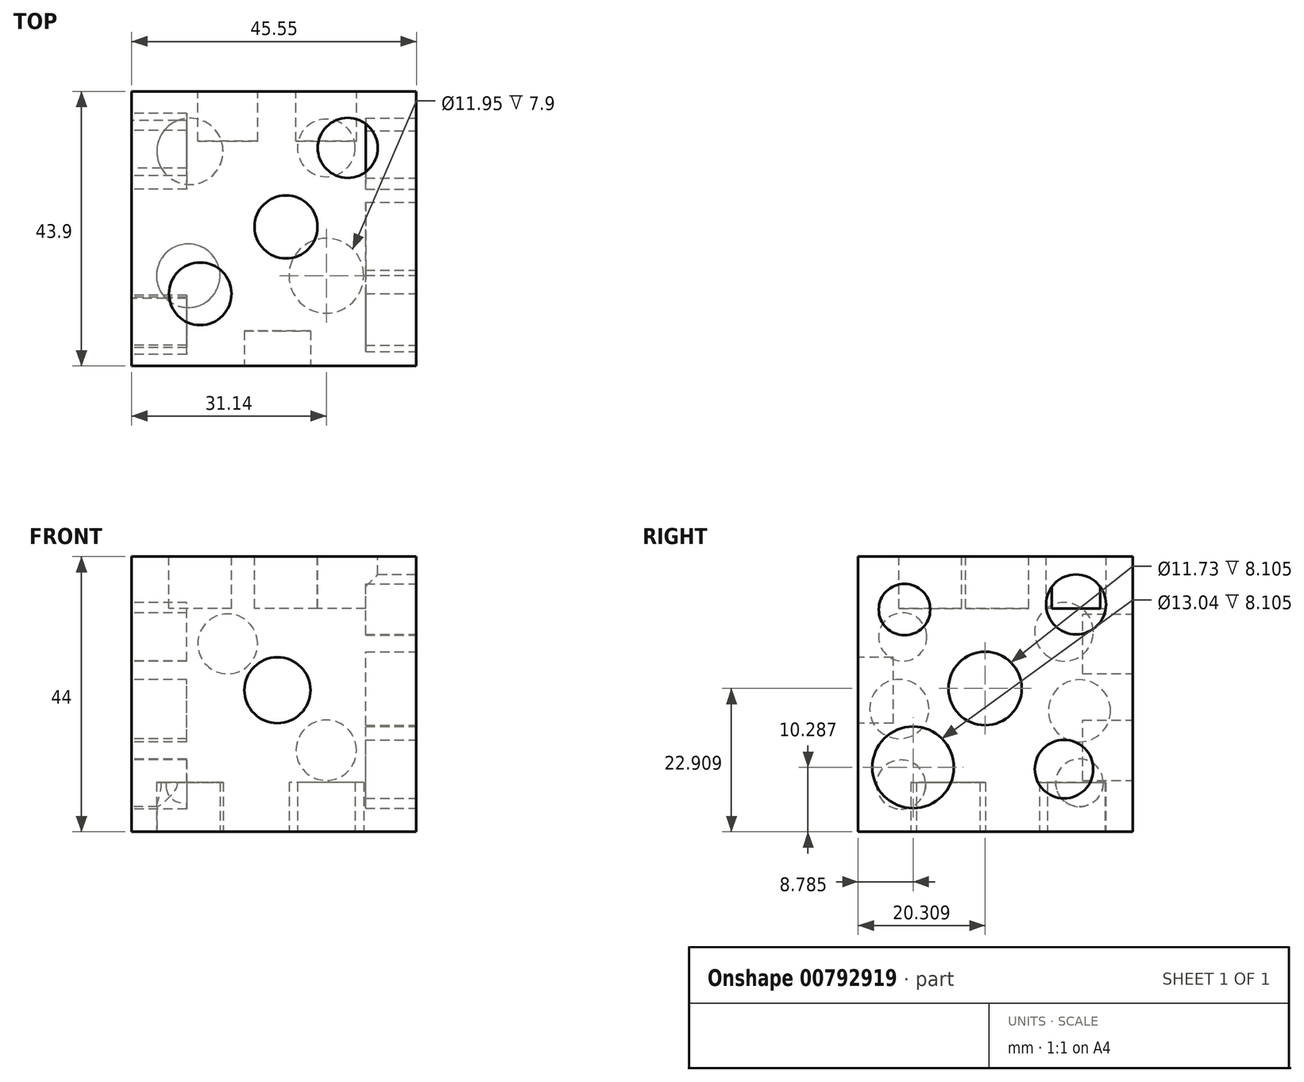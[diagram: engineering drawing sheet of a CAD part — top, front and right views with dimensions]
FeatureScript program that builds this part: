
annotation { "Feature Type Name" : "Feature", "Feature Type Description" : "" }
export const myFeature = defineFeature(function(context is Context, id is Id, definition is map)
    precondition{}
    {
        {
            var Q0;
            Q0=qCreatedBy(makeId("Top.planeOp"),FACE);
            var sketch = newSketch(context, id + "F0", { "sketchPlane" : qUnion([Q0])});
            skLineSegment(sketch, "E0.bottom", {"start": v(14.4, 29.5) * mm, "end": v(-31.14, 29.5) * mm});
            skLineSegment(sketch, "E0.top", {"start": v(14.4, -14.4) * mm, "end": v(-31.14, -14.4) * mm});
            skLineSegment(sketch, "E0.left", {"start": v(14.4, 29.5) * mm, "end": v(14.4, -14.4) * mm});
            skLineSegment(sketch, "E0.right", {"start": v(-31.14, 29.5) * mm, "end": v(-31.14, -14.4) * mm});
            skPoint(sketch, "E0.middle", {"position": v(-8.37, 7.54) * mm});
            skSolve(sketch);
        }
        {
            var Q0;
            Q0=makeQuery(id+"F0.imprint","IMPRINT",FACE,{"disambiguationData":[TD([[makeQuery(id+"F0.imprint","IMPRINT",EDGE,{"derivedFrom":sQuery(id+"F0.wireOp",EDGE,"E0.bottom")}),1.0]])]});
            extrude(context, id + "F1", {"entities" : qUnion([Q0]), "depth" : 44 * mm, "offsetDistance" : 25 * mm});
        }
        {
            var Q0;
            Q0=qCreatedBy(makeId("Front.planeOp"),FACE);
            cPlane(context, id + "F2", {"entities" : qUnion([Q0]), "cplaneType" : CPlaneType.OFFSET, "offset" : 14.9 * mm, "width" : 150 * mm, "height" : 150 * mm});
        }
        {
            var Q0;
            Q0=qCreatedBy(id+"F2.planeOp",FACE);
            var sketch = newSketch(context, id + "F3", { "sketchPlane" : qUnion([Q0])});
            skCircle(sketch, "E1", {"center": v(-7.82, 22.63) * mm, "radius": 5.28 * mm});
            skSolve(sketch);
        }
        {
            var Q0;
            Q0=makeQuery(id+"F3.imprint","IMPRINT",FACE,{"disambiguationData":[TD([[makeQuery(id+"F3.imprint","IMPRINT",EDGE,{"derivedFrom":sQuery(id+"F3.wireOp",EDGE,"E1")}),1.0]])]});
            extrude(context, id + "F4", {"entities" : qUnion([Q0]), "operationType" : NewBodyOperationType.REMOVE, "oppositeDirection" : true, "depth" : 6.1 * mm, "offsetDistance" : 25 * mm});
        }
        {
            var Q0;
            Q0=qCreatedBy(makeId("Front.planeOp"),FACE);
            cPlane(context, id + "F5", {"entities" : qUnion([Q0]), "cplaneType" : CPlaneType.OFFSET, "offset" : 30.2 * mm, "oppositeDirection" : true, "width" : 150 * mm, "height" : 150 * mm});
        }
        {
            var Q0;
            Q0=qCreatedBy(id+"F5.planeOp",FACE);
            var sketch = newSketch(context, id + "F6", { "sketchPlane" : qUnion([Q0])});
            skCircle(sketch, "E2", {"center": v(-15.78, 30.04) * mm, "radius": 4.8 * mm});
            skCircle(sketch, "E3", {"center": v(0, 13.03) * mm, "radius": 4.83 * mm});
            skSolve(sketch);
        }
        {
            var Q0;
            Q0=makeQuery(id+"F6.imprint","IMPRINT",FACE,{"disambiguationData":[TD([[makeQuery(id+"F6.imprint","IMPRINT",EDGE,{"derivedFrom":sQuery(id+"F6.wireOp",EDGE,"E2")}),1.0]])]});
            var Q1;
            Q1=makeQuery(id+"F6.imprint","IMPRINT",FACE,{"disambiguationData":[TD([[makeQuery(id+"F6.imprint","IMPRINT",EDGE,{"derivedFrom":sQuery(id+"F6.wireOp",EDGE,"E3")}),1.0]])]});
            extrude(context, id + "F7", {"entities" : qUnion([Q0, Q1]), "operationType" : NewBodyOperationType.REMOVE, "depth" : 8.7 * mm, "offsetDistance" : 25 * mm});
        }
        {
            var Q0;
            Q0=qCreatedBy(makeId("Top.planeOp"),FACE);
            cPlane(context, id + "F8", {"entities" : qUnion([Q0]), "cplaneType" : CPlaneType.OFFSET, "offset" : 45.6 * mm, "width" : 150 * mm, "height" : 150 * mm});
        }
        {
            var Q0;
            Q0=qCreatedBy(id+"F8.planeOp",FACE);
            var sketch = newSketch(context, id + "F9", { "sketchPlane" : qUnion([Q0])});
            skCircle(sketch, "E4", {"center": v(-20.16, -2.88) * mm, "radius": 5 * mm});
            skCircle(sketch, "E5", {"center": v(-6.45, 7.82) * mm, "radius": 5.04 * mm});
            skCircle(sketch, "E6", {"center": v(3.43, 20.44) * mm, "radius": 4.8 * mm});
            skSolve(sketch);
        }
        {
            var Q0;
            Q0=makeQuery(id+"F9.imprint","IMPRINT",FACE,{"disambiguationData":[TD([[makeQuery(id+"F9.imprint","IMPRINT",EDGE,{"derivedFrom":sQuery(id+"F9.wireOp",EDGE,"E4")}),1.0]])]});
            var Q1;
            Q1=makeQuery(id+"F9.imprint","IMPRINT",FACE,{"disambiguationData":[TD([[makeQuery(id+"F9.imprint","IMPRINT",EDGE,{"derivedFrom":sQuery(id+"F9.wireOp",EDGE,"E5")}),1.0]])]});
            var Q2;
            Q2=makeQuery(id+"F9.imprint","IMPRINT",FACE,{"disambiguationData":[TD([[makeQuery(id+"F9.imprint","IMPRINT",EDGE,{"derivedFrom":sQuery(id+"F9.wireOp",EDGE,"E6")}),1.0]])]});
            var Q3;
            Q3=sQuery(id+"F9.wireOp",EDGE,"E4");
            var Q4;
            Q4=sQuery(id+"F9.wireOp",EDGE,"E5");
            var Q5;
            Q5=sQuery(id+"F9.wireOp",EDGE,"E6");
            extrude(context, id + "F10", {"entities" : qUnion([Q0, Q1, Q2]), "operationType" : NewBodyOperationType.REMOVE, "surfaceEntities" : qUnion([Q3, Q4, Q5]), "oppositeDirection" : true, "depth" : 9.9 * mm, "offsetDistance" : 25 * mm});
        }
        {
            var Q0;
            Q0=qCreatedBy(makeId("Top.planeOp"),FACE);
            var sketch = newSketch(context, id + "F11", { "sketchPlane" : qUnion([Q0])});
            skCircle(sketch, "E7", {"center": v(-21.81, 19.9) * mm, "radius": 5.3 * mm});
            skCircle(sketch, "E8", {"center": v(-22.09, 0) * mm, "radius": 5.08 * mm});
            skCircle(sketch, "E9", {"center": v(0, 20.44) * mm, "radius": 4.6 * mm});
            skCircle(sketch, "E10", {"center": v(0, 0) * mm, "radius": 5.97 * mm});
            skSolve(sketch);
        }
        {
            var Q0;
            Q0=makeQuery(id+"F11.imprint","IMPRINT",FACE,{"disambiguationData":[TD([[makeQuery(id+"F11.imprint","IMPRINT",EDGE,{"derivedFrom":sQuery(id+"F11.wireOp",EDGE,"E7")}),1.0]])]});
            var Q1;
            Q1=makeQuery(id+"F11.imprint","IMPRINT",FACE,{"disambiguationData":[TD([[makeQuery(id+"F11.imprint","IMPRINT",EDGE,{"derivedFrom":sQuery(id+"F11.wireOp",EDGE,"E8")}),1.0]])]});
            var Q2;
            Q2=makeQuery(id+"F11.imprint","IMPRINT",FACE,{"disambiguationData":[TD([[makeQuery(id+"F11.imprint","IMPRINT",EDGE,{"derivedFrom":sQuery(id+"F11.wireOp",EDGE,"E9")}),1.0]])]});
            var Q3;
            Q3=makeQuery(id+"F11.imprint","IMPRINT",FACE,{"disambiguationData":[TD([[makeQuery(id+"F11.imprint","IMPRINT",EDGE,{"derivedFrom":sQuery(id+"F11.wireOp",EDGE,"E10")}),1.0]])]});
            extrude(context, id + "F12", {"entities" : qUnion([Q0, Q1, Q2, Q3]), "operationType" : NewBodyOperationType.REMOVE, "depth" : 7.9 * mm, "offsetDistance" : 25 * mm});
        }
        {
            var Q0;
            Q0=qCreatedBy(makeId("Right.planeOp"),FACE);
            cPlane(context, id + "F13", {"entities" : qUnion([Q0]), "cplaneType" : CPlaneType.OFFSET, "offset" : 14.6 * mm, "width" : 150 * mm, "height" : 150 * mm});
        }
        {
            var Q0;
            Q0=qCreatedBy(id+"F13.planeOp",FACE);
            var sketch = newSketch(context, id + "F14", { "sketchPlane" : qUnion([Q0])});
            skCircle(sketch, "E11", {"center": v(-7, 35.53) * mm, "radius": 4.12 * mm});
            skCircle(sketch, "E12", {"center": v(20.44, 36.35) * mm, "radius": 4.8 * mm});
            skCircle(sketch, "E13", {"center": v(5.9, 22.9) * mm, "radius": 5.87 * mm});
            skCircle(sketch, "E14", {"center": v(-5.63, 10.29) * mm, "radius": 6.52 * mm});
            skCircle(sketch, "E15", {"center": v(18.52, 10.01) * mm, "radius": 4.67 * mm});
            skSolve(sketch);
        }
        {
            var Q0;
            Q0=makeQuery(id+"F14.imprint","IMPRINT",FACE,{"disambiguationData":[TD([[makeQuery(id+"F14.imprint","IMPRINT",EDGE,{"derivedFrom":sQuery(id+"F14.wireOp",EDGE,"E11")}),1.0]])]});
            var Q1;
            Q1=makeQuery(id+"F14.imprint","IMPRINT",FACE,{"disambiguationData":[TD([[makeQuery(id+"F14.imprint","IMPRINT",EDGE,{"derivedFrom":sQuery(id+"F14.wireOp",EDGE,"E12")}),1.0]])]});
            var Q2;
            Q2=makeQuery(id+"F14.imprint","IMPRINT",FACE,{"disambiguationData":[TD([[makeQuery(id+"F14.imprint","IMPRINT",EDGE,{"derivedFrom":sQuery(id+"F14.wireOp",EDGE,"E13")}),1.0]])]});
            var Q3;
            Q3=makeQuery(id+"F14.imprint","IMPRINT",FACE,{"disambiguationData":[TD([[makeQuery(id+"F14.imprint","IMPRINT",EDGE,{"derivedFrom":sQuery(id+"F14.wireOp",EDGE,"E14")}),1.0]])]});
            var Q4;
            Q4=makeQuery(id+"F14.imprint","IMPRINT",FACE,{"disambiguationData":[TD([[makeQuery(id+"F14.imprint","IMPRINT",EDGE,{"derivedFrom":sQuery(id+"F14.wireOp",EDGE,"E15")}),1.0]])]});
            extrude(context, id + "F15", {"entities" : qUnion([Q0, Q1, Q2, Q3, Q4]), "operationType" : NewBodyOperationType.REMOVE, "oppositeDirection" : true, "depth" : 8.3 * mm, "offsetDistance" : 25 * mm});
        }
        {
            var Q0;
            Q0=qCreatedBy(makeId("Right.planeOp"),FACE);
            cPlane(context, id + "F16", {"entities" : qUnion([Q0]), "cplaneType" : CPlaneType.OFFSET, "offset" : 31.3 * mm, "oppositeDirection" : true, "width" : 150 * mm, "height" : 150 * mm});
        }
        {
            var Q0;
            Q0=qCreatedBy(id+"F16.planeOp",FACE);
            var sketch = newSketch(context, id + "F17", { "sketchPlane" : qUnion([Q0])});
            skCircle(sketch, "E16", {"center": v(-7.55, 7.55) * mm, "radius": 3.93 * mm});
            skCircle(sketch, "E17", {"center": v(-7.82, 19.62) * mm, "radius": 4.74 * mm});
            skCircle(sketch, "E18", {"center": v(-7.27, 31.15) * mm, "radius": 3.85 * mm});
            skCircle(sketch, "E19", {"center": v(21, 7.82) * mm, "radius": 3.81 * mm});
            skCircle(sketch, "E20", {"center": v(21, 19.35) * mm, "radius": 4.97 * mm});
            skCircle(sketch, "E21", {"center": v(18.52, 31.97) * mm, "radius": 4.69 * mm});
            skSolve(sketch);
        }
        {
            var Q0;
            Q0=makeQuery(id+"F17.imprint","IMPRINT",FACE,{"disambiguationData":[TD([[makeQuery(id+"F17.imprint","IMPRINT",EDGE,{"derivedFrom":sQuery(id+"F17.wireOp",EDGE,"E16")}),1.0]])]});
            var Q1;
            Q1=makeQuery(id+"F17.imprint","IMPRINT",FACE,{"disambiguationData":[TD([[makeQuery(id+"F17.imprint","IMPRINT",EDGE,{"derivedFrom":sQuery(id+"F17.wireOp",EDGE,"E17")}),1.0]])]});
            var Q2;
            Q2=makeQuery(id+"F17.imprint","IMPRINT",FACE,{"disambiguationData":[TD([[makeQuery(id+"F17.imprint","IMPRINT",EDGE,{"derivedFrom":sQuery(id+"F17.wireOp",EDGE,"E18")}),1.0]])]});
            var Q3;
            Q3=makeQuery(id+"F17.imprint","IMPRINT",FACE,{"disambiguationData":[TD([[makeQuery(id+"F17.imprint","IMPRINT",EDGE,{"derivedFrom":sQuery(id+"F17.wireOp",EDGE,"E19")}),1.0]])]});
            var Q4;
            Q4=makeQuery(id+"F17.imprint","IMPRINT",FACE,{"disambiguationData":[TD([[makeQuery(id+"F17.imprint","IMPRINT",EDGE,{"derivedFrom":sQuery(id+"F17.wireOp",EDGE,"E20")}),1.0]])]});
            var Q5;
            Q5=makeQuery(id+"F17.imprint","IMPRINT",FACE,{"disambiguationData":[TD([[makeQuery(id+"F17.imprint","IMPRINT",EDGE,{"derivedFrom":sQuery(id+"F17.wireOp",EDGE,"E21")}),1.0]])]});
            extrude(context, id + "F18", {"entities" : qUnion([Q0, Q1, Q2, Q3, Q4, Q5]), "operationType" : NewBodyOperationType.REMOVE, "depth" : 9 * mm, "offsetDistance" : 25 * mm});
        }
    });
